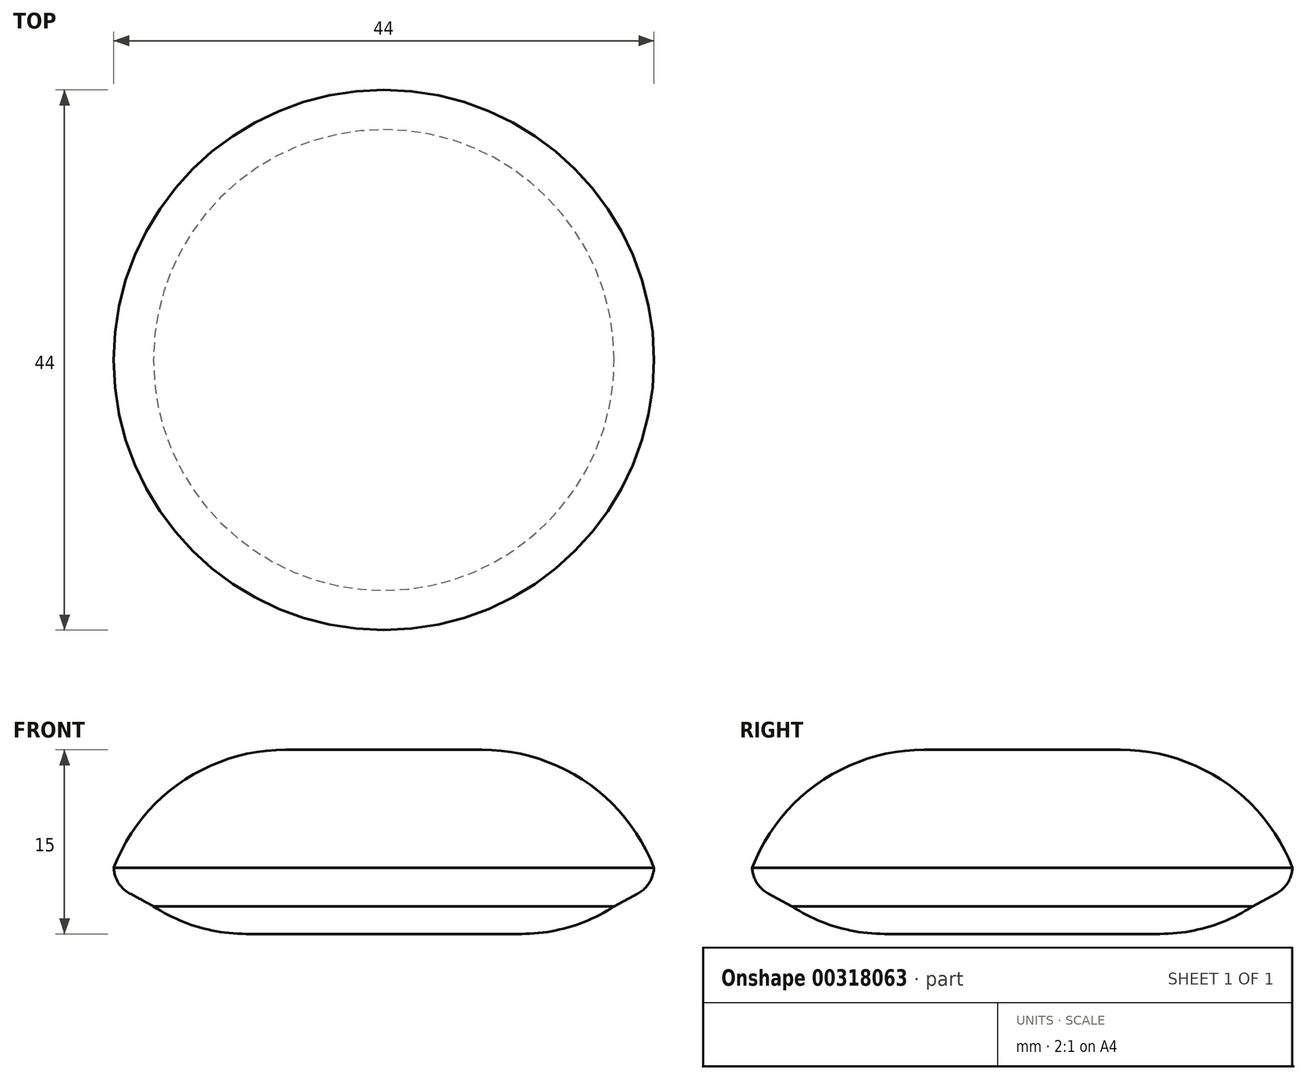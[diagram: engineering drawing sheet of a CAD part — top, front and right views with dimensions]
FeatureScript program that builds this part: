
annotation { "Feature Type Name" : "Feature", "Feature Type Description" : "" }
export const myFeature = defineFeature(function(context is Context, id is Id, definition is map)
    precondition{}
    {
        {
            var Q0;
            Q0=qCreatedBy(makeId("Front.planeOp"),FACE);
            var sketch = newSketch(context, id + "F0", { "sketchPlane" : qUnion([Q0])});
            skLineSegment(sketch, "E0", {"start": v(0, 0) * mm, "end": v(8, 0) * mm});
            skArc(sketch, "E1", {"start": v(22, -9.61) * mm, "mid": v(16.5, -2.64) * mm, "end": v(8, 0) * mm});
            skLineSegment(sketch, "E2", {"start": v(0, -12) * mm, "end": v(19.5, -12) * mm});
            skArc(sketch, "E3", {"start": v(19.5, -12) * mm, "mid": v(21.23, -11.3) * mm, "end": v(22, -9.61) * mm});
            skLineSegment(sketch, "E4", {"start": v(0, -15) * mm, "end": v(0, 0) * mm});
            skLineSegment(sketch, "E5", {"start": v(0, -15) * mm, "end": v(11.22, -15) * mm});
            skLineSegment(sketch, "E6", {"start": v(20.7, -11.7) * mm, "end": v(18.76, -12.75) * mm});
            skArc(sketch, "E7", {"start": v(11.22, -15) * mm, "mid": v(15.16, -14.43) * mm, "end": v(18.76, -12.75) * mm});
            skSolve(sketch);
        }
        {
            var Q0;
            Q0 = qSketchRegion(id + "F0", true);
            var Q1;
            Q1=sQuery(id+"F0.wireOp",EDGE,"E4");
            revolve(context, id + "F1", {"entities" : qUnion([Q0]), "axis" : qUnion([Q1]), "revolveType" : RevolveType.FULL});
        }
    });
